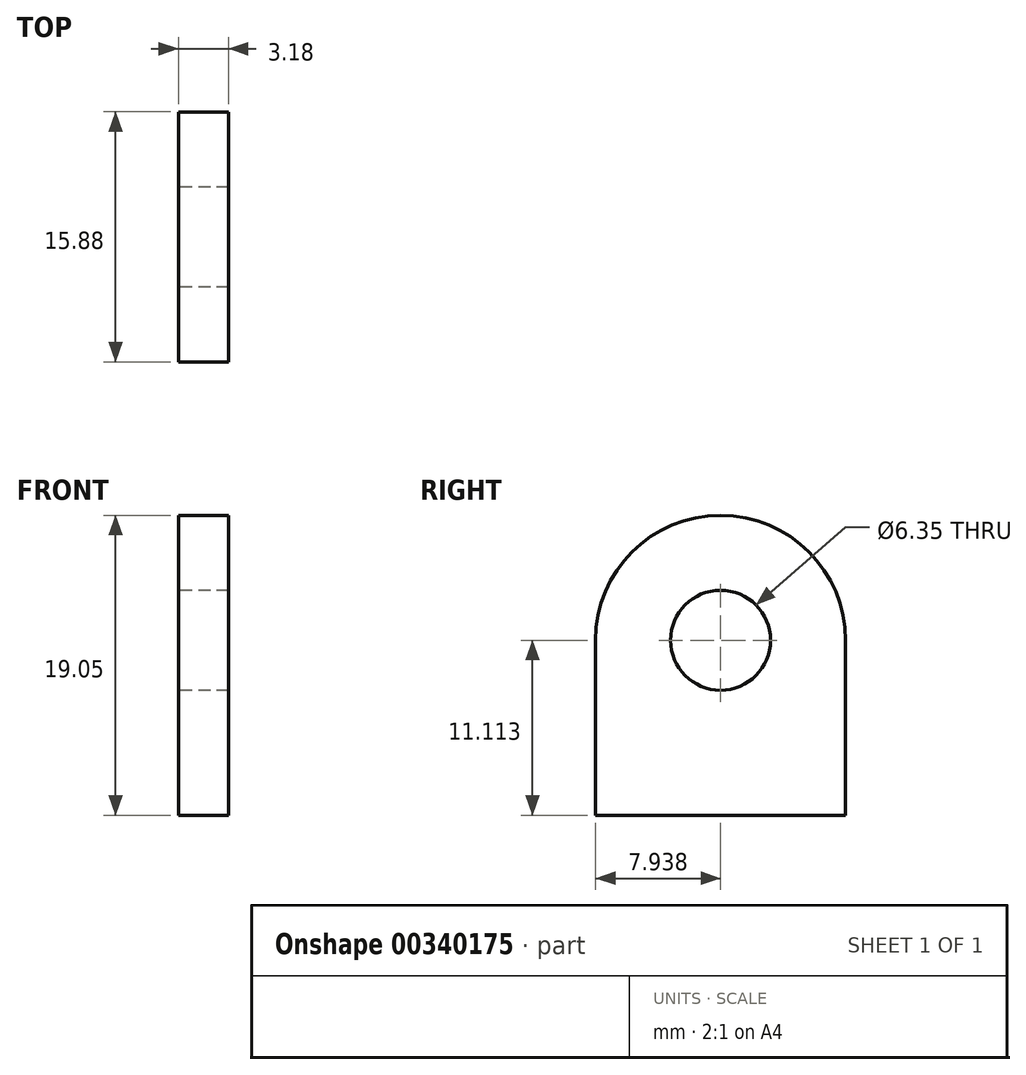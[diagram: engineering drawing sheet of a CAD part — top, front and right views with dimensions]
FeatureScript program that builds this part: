
annotation { "Feature Type Name" : "Feature", "Feature Type Description" : "" }
export const myFeature = defineFeature(function(context is Context, id is Id, definition is map)
    precondition{}
    {
        {
            var Q0;
            Q0=qCreatedBy(makeId("Right.planeOp"),FACE);
            var sketch = newSketch(context, id + "F0", { "sketchPlane" : qUnion([Q0])});
            skLineSegment(sketch, "E0.bottom", {"start": v(0, 0) * mm, "end": v(15.88, 0) * mm});
            skLineSegment(sketch, "E0.top", {"start": v(0, 11.11) * mm, "end": v(15.88, 11.11) * mm});
            skLineSegment(sketch, "E0.left", {"start": v(0, 0) * mm, "end": v(0, 11.11) * mm});
            skLineSegment(sketch, "E0.right", {"start": v(15.88, 0) * mm, "end": v(15.88, 11.11) * mm});
            skCircle(sketch, "E1", {"center": v(7.94, 11.11) * mm, "radius": 7.94 * mm});
            skCircle(sketch, "E2", {"center": v(7.94, 11.11) * mm, "radius": 3.18 * mm});
            skSolve(sketch);
        }
        {
            var Q0;
            Q0 = qSketchRegion(id + "F0", true);
            extrude(context, id + "F1", {"entities" : qUnion([Q0]), "depth" : 3.17 * mm});
        }
    });
